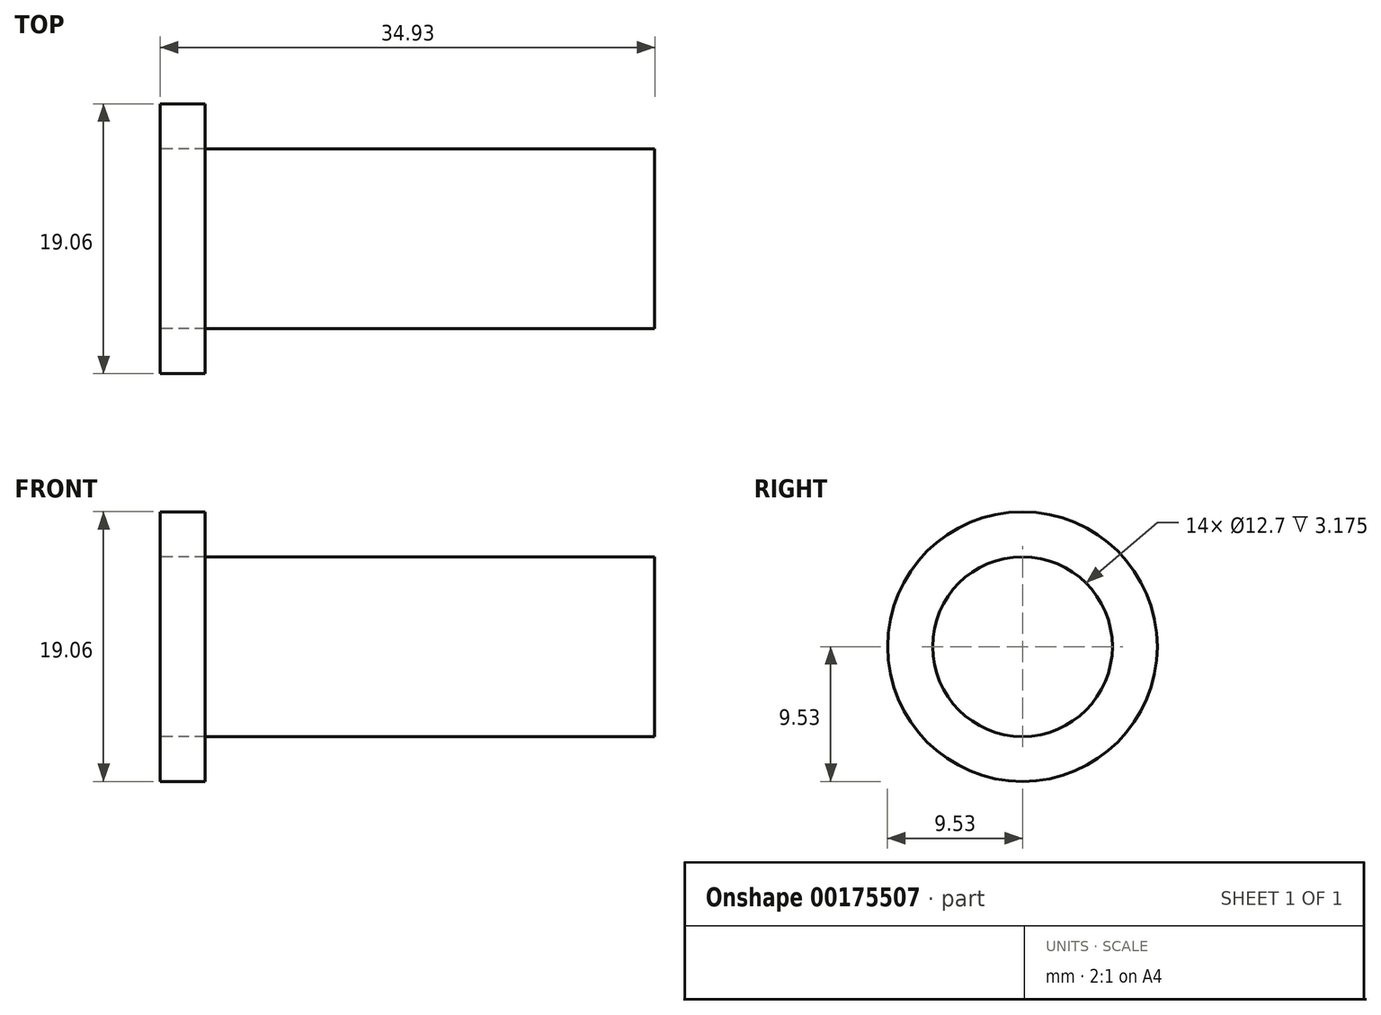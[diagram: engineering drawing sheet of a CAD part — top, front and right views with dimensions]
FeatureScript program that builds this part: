
annotation { "Feature Type Name" : "Feature", "Feature Type Description" : "" }
export const myFeature = defineFeature(function(context is Context, id is Id, definition is map)
    precondition{}
    {
        {
            var Q0;
            Q0=qCreatedBy(makeId("Right.planeOp"),FACE);
            var sketch = newSketch(context, id + "F0", { "sketchPlane" : qUnion([Q0])});
            skCircle(sketch, "E0", {"center": v(0, 0) * mm, "radius": 6.35 * mm});
            skSolve(sketch);
        }
        {
            var Q0;
            Q0=makeQuery(id+"F0.imprint","IMPRINT",FACE,{"disambiguationData":[TD([[makeQuery(id+"F0.imprint","IMPRINT",EDGE,{"derivedFrom":sQuery(id+"F0.wireOp",EDGE,"E0")}),1.0]])]});
            var Q1;
            Q1=sQuery(id+"F0.wireOp",EDGE,"E0");
            extrude(context, id + "F1", {"entities" : qUnion([Q0]), "surfaceEntities" : qUnion([Q1]), "depth" : 34.92 * mm});
        }
        {
            var Q0;
            Q0=makeQuery(id+"F1.opExtrude","CAP_FACE",FACE,{"disambiguationData":[OSD([sQuery(id+"F0.wireOp",EDGE,"E0")])],"isStart":true});
            var sketch = newSketch(context, id + "F2", { "sketchPlane" : qUnion([Q0])});
            skCircle(sketch, "E1", {"center": v(0, 0) * mm, "radius": 9.53 * mm});
            skSolve(sketch);
        }
        {
            var Q0;
            Q0=makeQuery(id+"F2.imprint","IMPRINT",FACE,{"disambiguationData":[TD([[makeQuery(id+"F2.imprint","IMPRINT",EDGE,{"derivedFrom":sQuery(id+"F2.wireOp",EDGE,"E1")}),1.0]])]});
            extrude(context, id + "F3", {"entities" : qUnion([Q0]), "oppositeDirection" : true, "depth" : 3.17 * mm});
        }
    });
